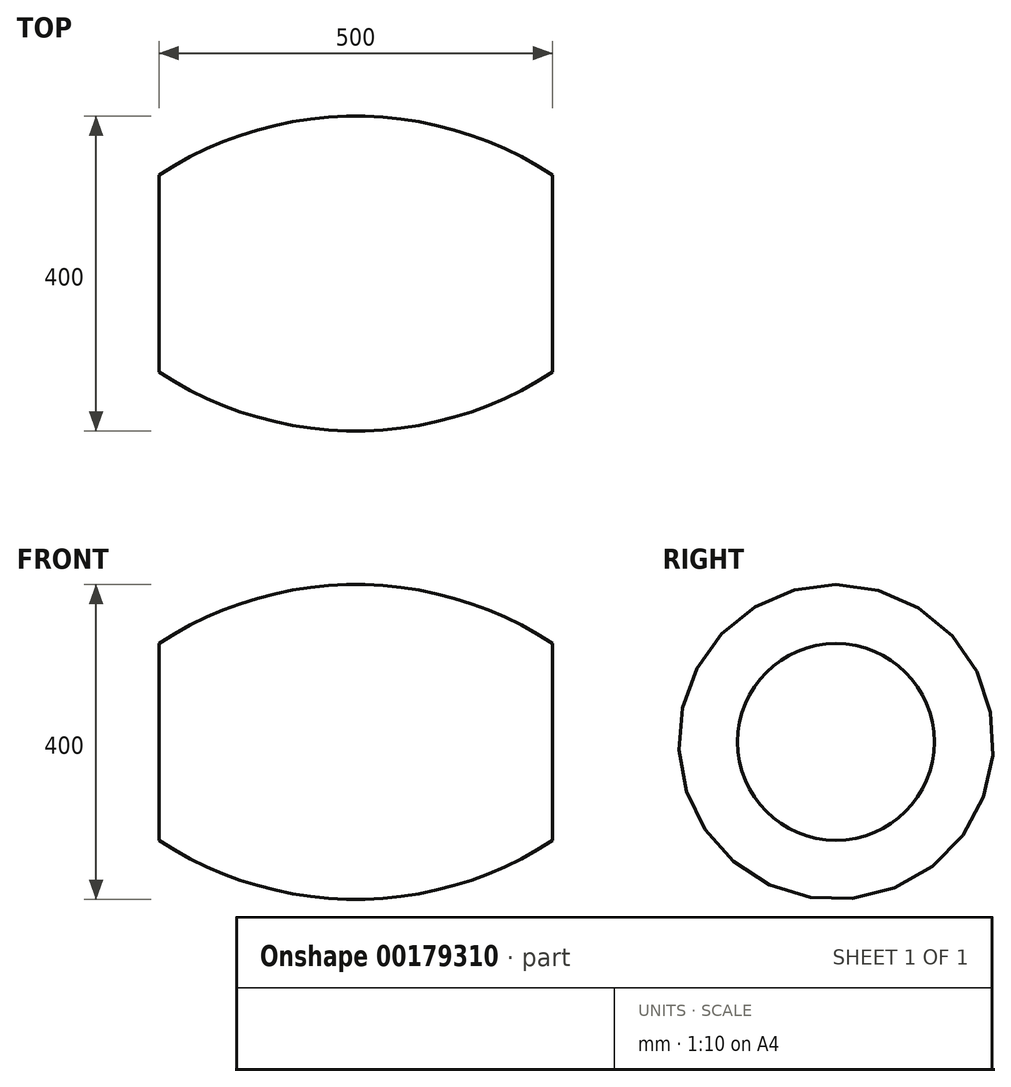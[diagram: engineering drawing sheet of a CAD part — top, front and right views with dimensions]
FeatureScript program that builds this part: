
annotation { "Feature Type Name" : "Feature", "Feature Type Description" : "" }
export const myFeature = defineFeature(function(context is Context, id is Id, definition is map)
    precondition{}
    {
        {
            var Q0;
            Q0=qCreatedBy(makeId("Front.planeOp"),FACE);
            var sketch = newSketch(context, id + "F0", { "sketchPlane" : qUnion([Q0])});
            skLineSegment(sketch, "E0", {"start": v(0, 125) * mm, "end": v(0, 0) * mm});
            skLineSegment(sketch, "E1", {"start": v(0, 0) * mm, "end": v(500, 0) * mm});
            skLineSegment(sketch, "E2", {"start": v(500, 0) * mm, "end": v(500, 125) * mm});
            skLineSegment(sketch, "E3", {"start": v(250, 0) * mm, "end": v(250, 200) * mm, "construction": true});
            skArc(sketch, "E4", {"start": v(500, 125) * mm, "mid": v(380.5, 180.85) * mm, "end": v(250, 200) * mm});
            skArc(sketch, "E5", {"start": v(250, 200) * mm, "mid": v(119.5, 180.85) * mm, "end": v(0, 125) * mm});
            skSolve(sketch);
        }
        {
            var Q0;
            Q0=makeQuery(id+"F0.imprint","IMPRINT",FACE,{"disambiguationData":[TD([[makeQuery(id+"F0.imprint","IMPRINT",EDGE,{"derivedFrom":sQuery(id+"F0.wireOp",EDGE,"E0")}),1.0]])]});
            var Q1;
            Q1=sQuery(id+"F0.wireOp",EDGE,"E1");
            revolve(context, id + "F1", {"entities" : qUnion([Q0]), "axis" : qUnion([Q1]), "revolveType" : RevolveType.FULL});
        }
    });
